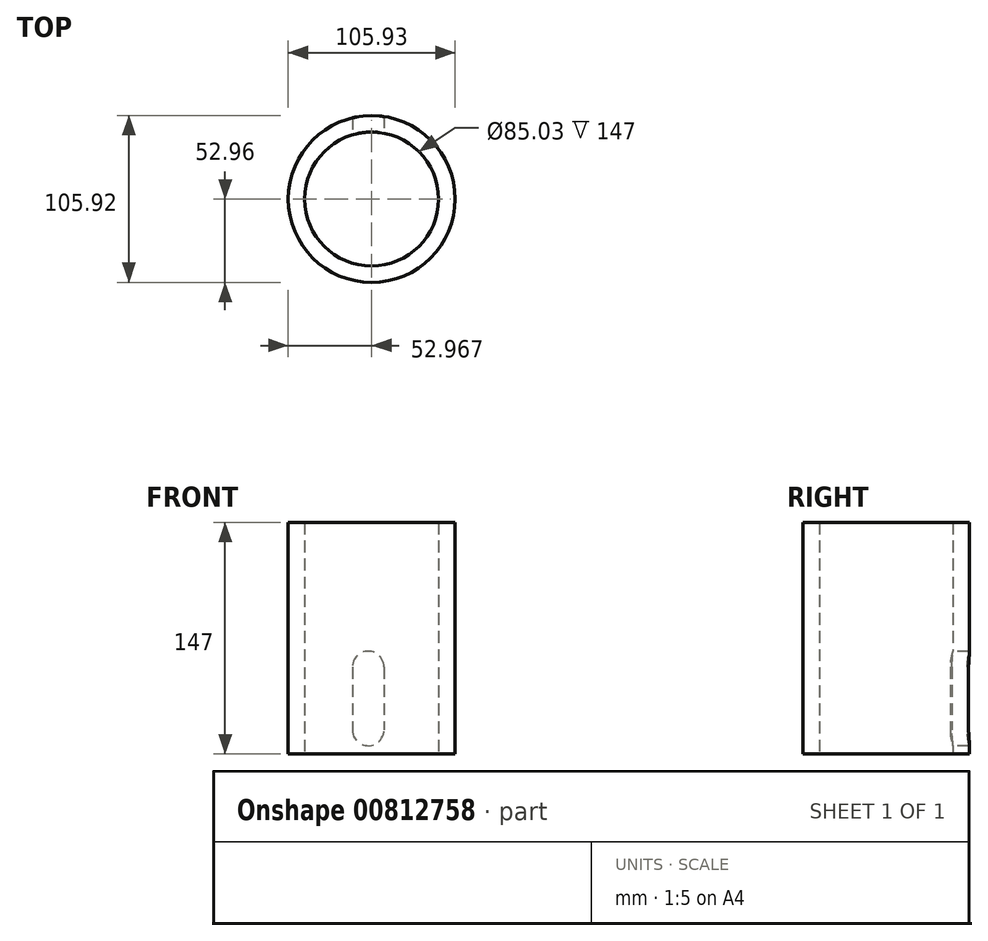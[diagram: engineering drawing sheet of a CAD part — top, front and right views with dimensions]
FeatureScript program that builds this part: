
annotation { "Feature Type Name" : "Feature", "Feature Type Description" : "" }
export const myFeature = defineFeature(function(context is Context, id is Id, definition is map)
    precondition{}
    {
        {
            var Q0;
            Q0=qCreatedBy(makeId("Top.planeOp"),FACE);
            var sketch = newSketch(context, id + "F0", { "sketchPlane" : qUnion([Q0])});
            skCircle(sketch, "E0", {"center": v(2.2, 0) * mm, "radius": 52.96 * mm});
            skCircle(sketch, "E1", {"center": v(2.2, 0) * mm, "radius": 42.51 * mm});
            skSolve(sketch);
        }
        {
            var Q0;
            Q0=makeQuery(id+"F0.imprint","IMPRINT",FACE,{"disambiguationData":[TD([[makeQuery(id+"F0.imprint","IMPRINT",EDGE,{"derivedFrom":sQuery(id+"F0.wireOp",EDGE,"E0")}),1.0]])]});
            extrude(context, id + "F1", {"entities" : qUnion([Q0]), "depth" : 147 * mm, "offsetDistance" : 25 * mm});
        }
        {
            var Q0;
            Q0=qCreatedBy(makeId("Front.planeOp"),FACE);
            var sketch = newSketch(context, id + "F2", { "sketchPlane" : qUnion([Q0])});
            skLineSegment(sketch, "E2.bottom", {"start": v(-10, 55.21) * mm, "end": v(10, 55.21) * mm});
            skLineSegment(sketch, "E2.top", {"start": v(-10, 15.21) * mm, "end": v(10, 15.21) * mm});
            skLineSegment(sketch, "E2.left", {"start": v(-10, 55.21) * mm, "end": v(-10, 15.21) * mm});
            skLineSegment(sketch, "E2.right", {"start": v(10, 55.21) * mm, "end": v(10, 15.21) * mm});
            skCircle(sketch, "E3", {"center": v(0, 55.21) * mm, "radius": 10 * mm});
            skCircle(sketch, "E4", {"center": v(0, 15.21) * mm, "radius": 10 * mm});
            skSolve(sketch);
        }
        {
            var Q0;
            {var subQ0=sQuery(id+"F2.wireOp",EDGE,"E2.left");Q0=makeQuery(id+"F2.imprint","IMPRINT",FACE,{"disambiguationData":[TD([[makeQuery(id+"F2.imprint","IMPRINT",EDGE,{"derivedFrom":subQ0}),1.0]])]});}
            var Q1;
            {var subQ0=sQuery(id+"F2.wireOp",EDGE,"E2.top");Q1=makeQuery(id+"F2.imprint","IMPRINT",FACE,{"disambiguationData":[TD([[makeQuery(id+"F2.imprint","IMPRINT",EDGE,{"derivedFrom":subQ0}),1.0]])]});}
            var Q2;
            {var subQ0=sQuery(id+"F2.wireOp",EDGE,"E2.bottom");Q2=makeQuery(id+"F2.imprint","IMPRINT",FACE,{"disambiguationData":[TD([[makeQuery(id+"F2.imprint","IMPRINT",EDGE,{"derivedFrom":subQ0}),-1.0]])]});}
            var Q3;
            {var subQ0=sQuery(id+"F2.wireOp",EDGE,"E2.top");Q3=makeQuery(id+"F2.imprint","IMPRINT",FACE,{"disambiguationData":[TD([[makeQuery(id+"F2.imprint","IMPRINT",EDGE,{"derivedFrom":subQ0}),-1.0]])]});}
            var Q4;
            {var subQ0=sQuery(id+"F2.wireOp",EDGE,"E2.bottom");Q4=makeQuery(id+"F2.imprint","IMPRINT",FACE,{"disambiguationData":[TD([[makeQuery(id+"F2.imprint","IMPRINT",EDGE,{"derivedFrom":subQ0}),1.0]])]});}
            var Q5;
            Q5=makeQuery(id+"F1.opExtrude","SWEPT_FACE",FACE,{"disambiguationData":[OSD([sQuery(id+"F0.wireOp",EDGE,"E0")])]});
            extrude(context, id + "F3", {"entities" : qUnion([Q0, Q1, Q2, Q3, Q4]), "operationType" : NewBodyOperationType.REMOVE, "endBound" : BoundingType.UP_TO_SURFACE, "oppositeDirection" : true, "depth" : 25 * mm, "endBoundEntityFace" : qUnion([Q5]), "offsetDistance" : 25 * mm});
        }
    });
